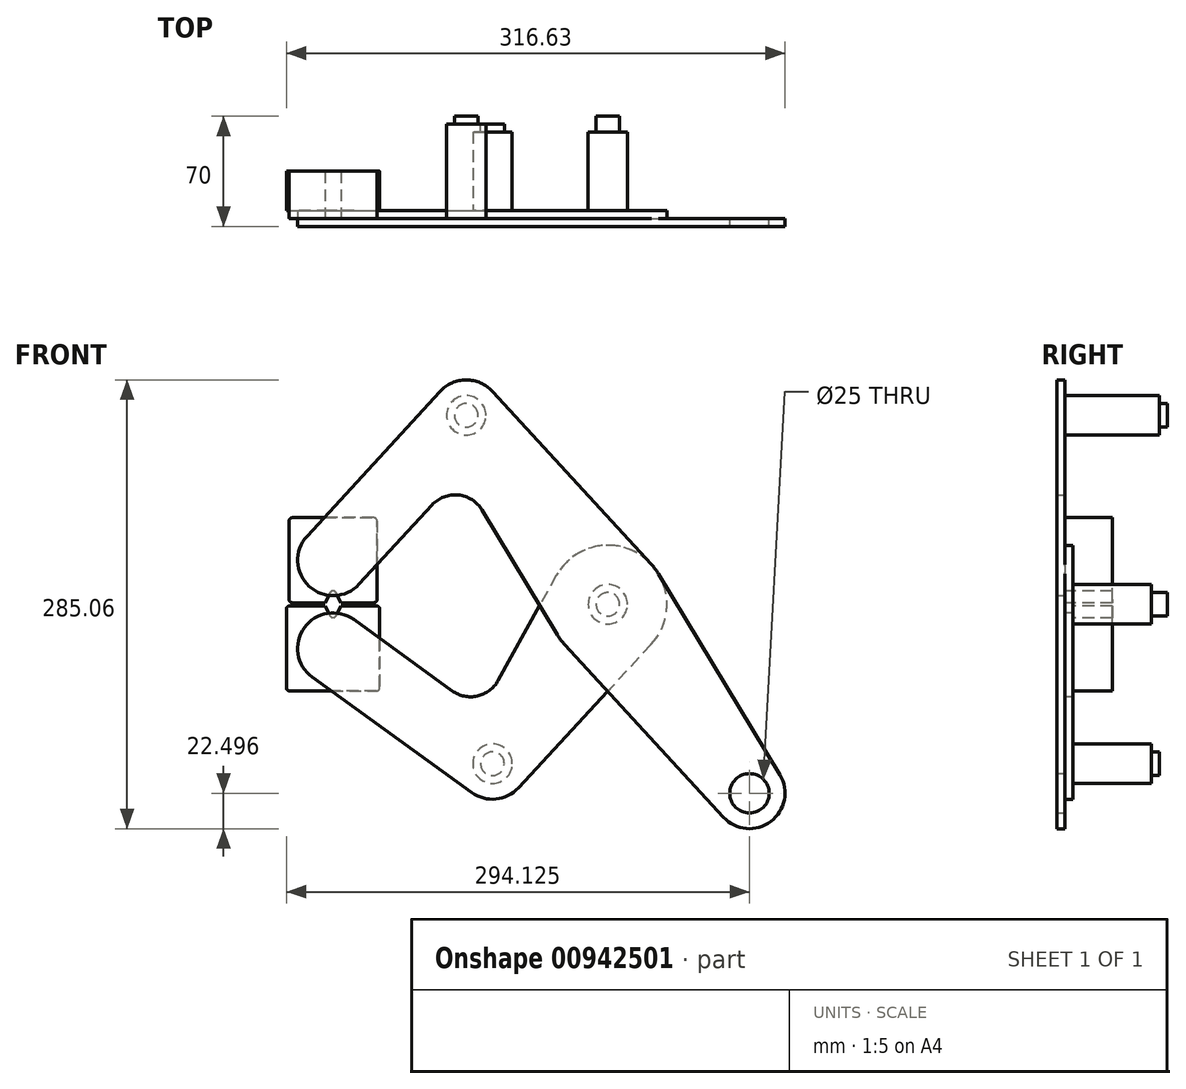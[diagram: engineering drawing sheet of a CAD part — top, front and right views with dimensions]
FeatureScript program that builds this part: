
annotation { "Feature Type Name" : "Feature", "Feature Type Description" : "" }
export const myFeature = defineFeature(function(context is Context, id is Id, definition is map)
    precondition{}
    {
        {
            var Q0;
            Q0=qCreatedBy(makeId("Front.planeOp"),FACE);
            var sketch = newSketch(context, id + "F0", { "sketchPlane" : qUnion([Q0])});
            skCircle(sketch, "E0", {"center": v(0, 0) * mm, "radius": 7.5 * mm});
            skCircle(sketch, "E1", {"center": v(89.96, -120.03) * mm, "radius": 7.5 * mm});
            skCircle(sketch, "E2", {"center": v(-89.96, 120.03) * mm, "radius": 7.5 * mm});
            skCircle(sketch, "E3", {"center": v(-174.54, 28) * mm, "radius": 7.5 * mm});
            skLineSegment(sketch, "E4", {"start": v(-89.96, 120.03) * mm, "end": v(-174.54, 28) * mm, "construction": true});
            skCircle(sketch, "E5", {"center": v(89.96, -120.03) * mm, "radius": 22.5 * mm});
            skCircle(sketch, "E6", {"center": v(-174.54, 28) * mm, "radius": 22.5 * mm});
            skCircle(sketch, "E7", {"center": v(-89.96, 120.03) * mm, "radius": 22.5 * mm});
            skLineSegment(sketch, "E8", {"start": v(-191.11, 43.23) * mm, "end": v(-106.52, 135.26) * mm});
            skLineSegment(sketch, "E9", {"start": v(-157.98, 12.78) * mm, "end": v(-111.77, 63.05) * mm});
            skCircle(sketch, "E10", {"center": v(0, 0) * mm, "radius": 37.5 * mm});
            skLineSegment(sketch, "E11", {"start": v(-73.39, 135.26) * mm, "end": v(27.6, 25.38) * mm});
            skLineSegment(sketch, "E12", {"start": v(-79.92, 59.85) * mm, "end": v(-32.1, -19.38) * mm});
            skLineSegment(sketch, "E13", {"start": v(-27.6, -25.38) * mm, "end": v(73.39, -135.26) * mm});
            skLineSegment(sketch, "E14", {"start": v(32.1, 19.38) * mm, "end": v(109.22, -108.4) * mm});
            skArc(sketch, "E15.filletArc", {"start": v(-79.92, 59.85) * mm, "mid": v(-95.04, 69.42) * mm, "end": v(-111.77, 63.05) * mm});
            skLineSegment(sketch, "E16", {"start": v(0, 0) * mm, "end": v(-73.27, -101.27) * mm, "construction": true});
            skLineSegment(sketch, "E17", {"start": v(-73.27, -101.27) * mm, "end": v(-174.54, -28) * mm, "construction": true});
            skCircle(sketch, "E18", {"center": v(-174.54, -28) * mm, "radius": 7.5 * mm});
            skCircle(sketch, "E19", {"center": v(-73.27, -101.27) * mm, "radius": 7.5 * mm});
            skCircle(sketch, "E20", {"center": v(-174.54, -28) * mm, "radius": 22.5 * mm});
            skCircle(sketch, "E21", {"center": v(-73.27, -101.27) * mm, "radius": 22.5 * mm});
            skLineSegment(sketch, "E22", {"start": v(-161.36, -9.77) * mm, "end": v(-98.93, -54.94) * mm});
            skLineSegment(sketch, "E23", {"start": v(-187.73, -46.23) * mm, "end": v(-86.46, -119.5) * mm});
            skLineSegment(sketch, "E24", {"start": v(-32.8, 18.18) * mm, "end": v(-69.71, -48.43) * mm});
            skLineSegment(sketch, "E25", {"start": v(27.52, -25.47) * mm, "end": v(-56.76, -116.55) * mm});
            skArc(sketch, "E26.filletArc", {"start": v(-98.93, -54.94) * mm, "mid": v(-82.85, -58.26) * mm, "end": v(-69.71, -48.43) * mm});
            skLineSegment(sketch, "E27", {"start": v(-89.96, 120.03) * mm, "end": v(89.96, -120.03) * mm, "construction": true});
            skLineSegment(sketch, "E28", {"start": v(0, 0) * mm, "end": v(-145.88, 0) * mm, "construction": true});
            skCircle(sketch, "E29", {"center": v(0, 0) * mm, "radius": 12.5 * mm});
            skCircle(sketch, "E30", {"center": v(89.96, -120.03) * mm, "radius": 12.5 * mm});
            skCircle(sketch, "E31", {"center": v(-73.27, -101.27) * mm, "radius": 12.5 * mm});
            skCircle(sketch, "E32", {"center": v(-89.96, 120.03) * mm, "radius": 12.5 * mm});
            skSolve(sketch);
        }
        {
            assignVariable(context, id + "F1", {"name" : "offsetdx", "anyValue" : 35});
        }
        {
            var Q0;
            {var subQ0=sQuery(id+"F0.wireOp",EDGE,"E8");Q0=makeQuery(id+"F0.imprint","IMPRINT",FACE,{"disambiguationData":[TD([[makeQuery(id+"F0.imprint","IMPRINT",EDGE,{"derivedFrom":subQ0}),-1.0]])]});}
            var Q1;
            Q1=makeQuery(id+"F0.imprint","IMPRINT",FACE,{"disambiguationData":[TD([[makeQuery(id+"F0.imprint","IMPRINT",EDGE,{"derivedFrom":sQuery(id+"F0.wireOp",EDGE,"E32")}),-1.0]])]});
            var Q2;
            Q2=makeQuery(id+"F0.imprint","IMPRINT",FACE,{"disambiguationData":[TD([[makeQuery(id+"F0.imprint","IMPRINT",EDGE,{"derivedFrom":sQuery(id+"F0.wireOp",EDGE,"E3")}),-1.0]])]});
            var Q3;
            Q3=makeQuery(id+"F0.imprint","IMPRINT",FACE,{"disambiguationData":[TD([[makeQuery(id+"F0.imprint","IMPRINT",EDGE,{"derivedFrom":sQuery(id+"F0.wireOp",EDGE,"E29")}),-1.0]])]});
            var Q4;
            {var subQ0=sQuery(id+"F0.wireOp",EDGE,"E13");var subQ1=sQuery(id+"F0.wireOp",EDGE,"E10");var subQ2=makeQuery(id+"F0.imprint","INTERSECT",VERTEX,{"derivedFrom":[subQ1,subQ0]});Q4=makeQuery(id+"F0.imprint","IMPRINT",FACE,{"disambiguationData":[TD([[makeQuery(id+"F0.imprint","IMPRINT",EDGE,{"disambiguationData":[TD([[subQ2,-1.0]])],"derivedFrom":subQ1}),-1.0]])]});}
            var Q5;
            {var subQ0=sQuery(id+"F0.wireOp",EDGE,"E14");Q5=makeQuery(id+"F0.imprint","IMPRINT",FACE,{"disambiguationData":[TD([[makeQuery(id+"F0.imprint","IMPRINT",EDGE,{"derivedFrom":subQ0}),-1.0]])]});}
            var Q6;
            Q6=makeQuery(id+"F0.imprint","IMPRINT",FACE,{"disambiguationData":[TD([[makeQuery(id+"F0.imprint","IMPRINT",EDGE,{"derivedFrom":sQuery(id+"F0.wireOp",EDGE,"E30")}),-1.0]])]});
            var Q7;
            {var subQ0=sQuery(id+"F0.wireOp",EDGE,"E12");var subQ1=sQuery(id+"F0.wireOp",EDGE,"E10");var subQ2=makeQuery(id+"F0.imprint","INTERSECT",VERTEX,{"derivedFrom":[subQ1,subQ0]});Q7=makeQuery(id+"F0.imprint","IMPRINT",FACE,{"disambiguationData":[TD([[makeQuery(id+"F0.imprint","IMPRINT",EDGE,{"disambiguationData":[TD([[subQ2,1.0]])],"derivedFrom":subQ1}),-1.0]])]});}
            var Q8;
            Q8=makeQuery(id+"F0.imprint","IMPRINT",FACE,{"disambiguationData":[TD([[makeQuery(id+"F0.imprint","IMPRINT",EDGE,{"derivedFrom":sQuery(id+"F0.wireOp",EDGE,"E0")}),-1.0]])]});
            var Q9;
            Q9=makeQuery(id+"F0.imprint","IMPRINT",FACE,{"disambiguationData":[TD([[makeQuery(id+"F0.imprint","IMPRINT",EDGE,{"derivedFrom":sQuery(id+"F0.wireOp",EDGE,"E2")}),-1.0]])]});
            extrude(context, id + "F2", {"entities" : qUnion([Q0, Q1, Q2, Q3, Q4, Q5, Q6, Q7, Q8, Q9]), "depth" : 5 * mm, "offsetDistance" : 25 * mm});
        }
        {
            var Q0;
            {var subQ0=sQuery(id+"F0.wireOp",EDGE,"E22");Q0=makeQuery(id+"F0.imprint","IMPRINT",FACE,{"disambiguationData":[TD([[makeQuery(id+"F0.imprint","IMPRINT",EDGE,{"derivedFrom":subQ0}),-1.0]])]});}
            var Q1;
            Q1=makeQuery(id+"F0.imprint","IMPRINT",FACE,{"disambiguationData":[TD([[makeQuery(id+"F0.imprint","IMPRINT",EDGE,{"derivedFrom":sQuery(id+"F0.wireOp",EDGE,"E29")}),-1.0]])]});
            var Q2;
            {var subQ0=sQuery(id+"F0.wireOp",EDGE,"E13");var subQ1=sQuery(id+"F0.wireOp",EDGE,"E10");var subQ2=makeQuery(id+"F0.imprint","INTERSECT",VERTEX,{"derivedFrom":[subQ1,subQ0]});Q2=makeQuery(id+"F0.imprint","IMPRINT",FACE,{"disambiguationData":[TD([[makeQuery(id+"F0.imprint","IMPRINT",EDGE,{"disambiguationData":[TD([[subQ2,-1.0]])],"derivedFrom":subQ1}),-1.0]])]});}
            var Q3;
            Q3=makeQuery(id+"F0.imprint","IMPRINT",FACE,{"disambiguationData":[TD([[makeQuery(id+"F0.imprint","IMPRINT",EDGE,{"derivedFrom":sQuery(id+"F0.wireOp",EDGE,"E31")}),-1.0]])]});
            var Q4;
            Q4=makeQuery(id+"F0.imprint","IMPRINT",FACE,{"disambiguationData":[TD([[makeQuery(id+"F0.imprint","IMPRINT",EDGE,{"derivedFrom":sQuery(id+"F0.wireOp",EDGE,"E18")}),-1.0]])]});
            var Q5;
            {var subQ0=sQuery(id+"F0.wireOp",EDGE,"E12");var subQ1=sQuery(id+"F0.wireOp",EDGE,"E10");var subQ2=makeQuery(id+"F0.imprint","INTERSECT",VERTEX,{"derivedFrom":[subQ1,subQ0]});Q5=makeQuery(id+"F0.imprint","IMPRINT",FACE,{"disambiguationData":[TD([[makeQuery(id+"F0.imprint","IMPRINT",EDGE,{"disambiguationData":[TD([[subQ2,1.0]])],"derivedFrom":subQ1}),-1.0]])]});}
            var Q6;
            Q6=makeQuery(id+"F0.imprint","IMPRINT",FACE,{"disambiguationData":[TD([[makeQuery(id+"F0.imprint","IMPRINT",EDGE,{"derivedFrom":sQuery(id+"F0.wireOp",EDGE,"E19")}),-1.0]])]});
            var Q7;
            Q7=makeQuery(id+"F0.imprint","IMPRINT",FACE,{"disambiguationData":[TD([[makeQuery(id+"F0.imprint","IMPRINT",EDGE,{"derivedFrom":sQuery(id+"F0.wireOp",EDGE,"E0")}),-1.0]])]});
            extrude(context, id + "F3", {"entities" : qUnion([Q0, Q1, Q2, Q3, Q4, Q5, Q6, Q7]), "oppositeDirection" : true, "depth" : 5 * mm, "offsetDistance" : 25 * mm});
        }
        {
            var Q0;
            {var subQ0=sQuery(id+"F0.wireOp",EDGE,"E8");Q0=makeQuery(id+"F0.imprint","IMPRINT",FACE,{"disambiguationData":[TD([[makeQuery(id+"F0.imprint","IMPRINT",EDGE,{"derivedFrom":subQ0}),-1.0]])]});}
            var sketch = newSketch(context, id + "F4", { "sketchPlane" : qUnion([Q0])});
            skLineSegment(sketch, "E33.0", {"start": v(0, 0) * mm, "end": v(-145.88, 0) * mm});
            skPoint(sketch, "E34.0", {"position": v(-174.54, 28) * mm});
            skLineSegment(sketch, "E35", {"start": v(-174.54, 28) * mm, "end": v(-174.54, 1) * mm, "construction": true});
            skLineSegment(sketch, "E36.bottom", {"start": v(-202.44, 55) * mm, "end": v(-146.65, 55) * mm});
            skLineSegment(sketch, "E36.top", {"start": v(-202.44, 1) * mm, "end": v(-146.65, 1) * mm});
            skLineSegment(sketch, "E36.left", {"start": v(-202.44, 55) * mm, "end": v(-202.44, 1) * mm});
            skLineSegment(sketch, "E36.right", {"start": v(-146.65, 55) * mm, "end": v(-146.65, 1) * mm});
            skLineSegment(sketch, "E37", {"start": v(-174.54, 11) * mm, "end": v(-169.54, 1) * mm});
            skLineSegment(sketch, "E38", {"start": v(-174.54, 11) * mm, "end": v(-179.54, 1) * mm});
            skLineSegment(sketch, "E39", {"start": v(-179.54, 1) * mm, "end": v(-169.54, 1) * mm});
            skSolve(sketch);
        }
        {
            var Q0;
            Q0=makeQuery(id+"F3.opExtrude","CAP_FACE",FACE,{"disambiguationData":[OSD([sQuery(id+"F0.wireOp",EDGE,"E10"),sQuery(id+"F0.wireOp",EDGE,"E18"),sQuery(id+"F0.wireOp",EDGE,"E20"),sQuery(id+"F0.wireOp",EDGE,"E21"),sQuery(id+"F0.wireOp",EDGE,"E22"),sQuery(id+"F0.wireOp",EDGE,"E23"),sQuery(id+"F0.wireOp",EDGE,"E24"),sQuery(id+"F0.wireOp",EDGE,"E25"),sQuery(id+"F0.wireOp",EDGE,"E26.filletArc"),sQuery(id+"F0.wireOp",EDGE,"E29"),sQuery(id+"F0.wireOp",EDGE,"E31")])],"isStart":false});
            var sketch = newSketch(context, id + "F5", { "sketchPlane" : qUnion([Q0])});
            skCircle(sketch, "E40.0", {"center": v(174.54, -28) * mm, "radius": 7.5 * mm});
            skLineSegment(sketch, "E41.bottom", {"start": v(204.17, -1) * mm, "end": v(144.92, -1) * mm});
            skLineSegment(sketch, "E41.top", {"start": v(204.17, -55) * mm, "end": v(144.92, -55) * mm});
            skLineSegment(sketch, "E41.left", {"start": v(204.17, -1) * mm, "end": v(204.17, -55) * mm});
            skLineSegment(sketch, "E41.right", {"start": v(144.92, -1) * mm, "end": v(144.92, -55) * mm});
            skLineSegment(sketch, "E42", {"start": v(174.54, -28) * mm, "end": v(174.54, -1) * mm, "construction": true});
            skLineSegment(sketch, "E43", {"start": v(174.54, -11) * mm, "end": v(169.54, -1) * mm});
            skLineSegment(sketch, "E44", {"start": v(174.54, -11) * mm, "end": v(179.54, -1) * mm});
            skSolve(sketch);
        }
        {
            var Q0;
            Q0=makeQuery(id+"F2.opExtrude","CAP_FACE",FACE,{"disambiguationData":[OSD([sQuery(id+"F0.wireOp",EDGE,"E3"),sQuery(id+"F0.wireOp",EDGE,"E5"),sQuery(id+"F0.wireOp",EDGE,"E6"),sQuery(id+"F0.wireOp",EDGE,"E7"),sQuery(id+"F0.wireOp",EDGE,"E8"),sQuery(id+"F0.wireOp",EDGE,"E9"),sQuery(id+"F0.wireOp",EDGE,"E10"),sQuery(id+"F0.wireOp",EDGE,"E11"),sQuery(id+"F0.wireOp",EDGE,"E12"),sQuery(id+"F0.wireOp",EDGE,"E13"),sQuery(id+"F0.wireOp",EDGE,"E14"),sQuery(id+"F0.wireOp",EDGE,"E15.filletArc"),sQuery(id+"F0.wireOp",EDGE,"E29"),sQuery(id+"F0.wireOp",EDGE,"E30"),sQuery(id+"F0.wireOp",EDGE,"E32")])],"isStart":false});
            cPlane(context, id + "F6", {"entities" : qUnion([Q0]), "cplaneType" : CPlaneType.OFFSET, "offset" : (getVariable(context, 'offsetdx')) * mm, "oppositeDirection" : true, "width" : 150 * mm, "height" : 150 * mm});
        }
        {
            var Q0;
            Q0=makeQuery(id+"F0.imprint","IMPRINT",FACE,{"disambiguationData":[TD([[makeQuery(id+"F0.imprint","IMPRINT",EDGE,{"derivedFrom":sQuery(id+"F0.wireOp",EDGE,"E0")}),-1.0]])]});
            var Q1;
            Q1=makeQuery(id+"F0.imprint","IMPRINT",FACE,{"disambiguationData":[TD([[makeQuery(id+"F0.imprint","IMPRINT",EDGE,{"derivedFrom":sQuery(id+"F0.wireOp",EDGE,"E2")}),-1.0]])]});
            var Q2;
            Q2=qCreatedBy(id+"F6.planeOp",FACE);
            var Q3;
            Q3=makeQuery(id+"F2.opExtrude","CAP_FACE",FACE,{"disambiguationData":[OSD([sQuery(id+"F0.wireOp",EDGE,"E3"),sQuery(id+"F0.wireOp",EDGE,"E5"),sQuery(id+"F0.wireOp",EDGE,"E6"),sQuery(id+"F0.wireOp",EDGE,"E7"),sQuery(id+"F0.wireOp",EDGE,"E8"),sQuery(id+"F0.wireOp",EDGE,"E9"),sQuery(id+"F0.wireOp",EDGE,"E10"),sQuery(id+"F0.wireOp",EDGE,"E11"),sQuery(id+"F0.wireOp",EDGE,"E12"),sQuery(id+"F0.wireOp",EDGE,"E13"),sQuery(id+"F0.wireOp",EDGE,"E14"),sQuery(id+"F0.wireOp",EDGE,"E15.filletArc"),sQuery(id+"F0.wireOp",EDGE,"E29"),sQuery(id+"F0.wireOp",EDGE,"E30"),sQuery(id+"F0.wireOp",EDGE,"E32")])],"isStart":false});
            extrude(context, id + "F7", {"entities" : qUnion([Q0, Q1]), "endBound" : BoundingType.UP_TO_SURFACE, "oppositeDirection" : true, "depth" : 25 * mm, "endBoundEntityFace" : qUnion([Q2]), "offsetDistance" : 25 * mm, "hasSecondDirection" : true, "secondDirectionBound" : SecondDirectionBoundingType.UP_TO_SURFACE, "secondDirectionOppositeDirection" : false, "secondDirectionDepth" : 25 * mm, "secondDirectionBoundEntityFace" : qUnion([Q3])});
        }
        {
            var Q0;
            Q0=makeQuery(id+"F0.imprint","IMPRINT",FACE,{"disambiguationData":[TD([[makeQuery(id+"F0.imprint","IMPRINT",EDGE,{"derivedFrom":sQuery(id+"F0.wireOp",EDGE,"E19")}),-1.0]])]});
            var Q1;
            Q1=qCreatedBy(id+"F6.planeOp",FACE);
            extrude(context, id + "F8", {"entities" : qUnion([Q0]), "endBound" : BoundingType.UP_TO_SURFACE, "oppositeDirection" : true, "depth" : 25 * mm, "endBoundEntityFace" : qUnion([Q1]), "offsetDistance" : 25 * mm});
        }
        {
            var Q0;
            {var subQ0=sQuery(id+"F4.wireOp",EDGE,"E36.left");Q0=makeQuery(id+"F4.imprint","IMPRINT",FACE,{"disambiguationData":[TD([[makeQuery(id+"F4.imprint","IMPRINT",EDGE,{"derivedFrom":subQ0}),1.0]])]});}
            var Q1;
            {var subQ4=sQuery(id+"F4.wireOp",EDGE,"E36.right");var subQ5=sQuery(id+"F4.wireOp",EDGE,"E36.bottom");var subQ6=makeQuery(id+"F4.imprint","INTERSECT",VERTEX,{"derivedFrom":[subQ5,subQ4]});Q1=makeQuery(id+"F4.imprint","IMPRINT",FACE,{"disambiguationData":[TD([[makeQuery(id+"F4.imprint","IMPRINT",EDGE,{"disambiguationData":[TD([[subQ6,1.0]])],"derivedFrom":subQ5}),-1.0]])]});}
            var Q2;
            Q2=qCreatedBy(id+"F6.planeOp",FACE);
            extrude(context, id + "F9", {"entities" : qUnion([Q0, Q1]), "endBound" : BoundingType.UP_TO_SURFACE, "oppositeDirection" : true, "depth" : 25 * mm, "endBoundEntityFace" : qUnion([Q2]), "offsetDistance" : 25 * mm});
        }
        {
            var Q0;
            Q0=makeQuery(id+"F0.imprint","IMPRINT",FACE,{"disambiguationData":[TD([[makeQuery(id+"F0.imprint","IMPRINT",EDGE,{"derivedFrom":sQuery(id+"F0.wireOp",EDGE,"E3")}),1.0]])]});
            var Q1;
            Q1=makeQuery(id+"F2.opExtrude","CAP_FACE",FACE,{"disambiguationData":[OSD([sQuery(id+"F0.wireOp",EDGE,"E3"),sQuery(id+"F0.wireOp",EDGE,"E5"),sQuery(id+"F0.wireOp",EDGE,"E6"),sQuery(id+"F0.wireOp",EDGE,"E7"),sQuery(id+"F0.wireOp",EDGE,"E8"),sQuery(id+"F0.wireOp",EDGE,"E9"),sQuery(id+"F0.wireOp",EDGE,"E10"),sQuery(id+"F0.wireOp",EDGE,"E11"),sQuery(id+"F0.wireOp",EDGE,"E12"),sQuery(id+"F0.wireOp",EDGE,"E13"),sQuery(id+"F0.wireOp",EDGE,"E14"),sQuery(id+"F0.wireOp",EDGE,"E15.filletArc"),sQuery(id+"F0.wireOp",EDGE,"E29"),sQuery(id+"F0.wireOp",EDGE,"E30"),sQuery(id+"F0.wireOp",EDGE,"E32")])],"isStart":false});
            extrude(context, id + "F10", {"entities" : qUnion([Q0]), "operationType" : NewBodyOperationType.ADD, "endBound" : BoundingType.UP_TO_SURFACE, "depth" : 25 * mm, "endBoundEntityFace" : qUnion([Q1]), "offsetDistance" : 25 * mm});
        }
        {
            var Q0;
            Q0=makeQuery(id+"F5.imprint","IMPRINT",FACE,{"disambiguationData":[TD([[makeQuery(id+"F5.imprint","IMPRINT",EDGE,{"derivedFrom":sQuery(id+"F5.wireOp",EDGE,"E40.0")}),1.0]])]});
            var Q1;
            {var subQ5=sQuery(id+"F5.wireOp",EDGE,"E41.left");Q1=makeQuery(id+"F5.imprint","IMPRINT",FACE,{"disambiguationData":[TD([[makeQuery(id+"F5.imprint","IMPRINT",EDGE,{"derivedFrom":subQ5}),-1.0]])]});}
            var Q2;
            {var subQ5=sQuery(id+"F5.wireOp",EDGE,"E41.bottom");var subQ7=sQuery(id+"F5.wireOp",EDGE,"E41.right");var subQ8=makeQuery(id+"F5.imprint","INTERSECT",VERTEX,{"derivedFrom":[subQ5,subQ7]});Q2=makeQuery(id+"F5.imprint","IMPRINT",FACE,{"disambiguationData":[TD([[makeQuery(id+"F5.imprint","IMPRINT",EDGE,{"disambiguationData":[TD([[subQ8,1.0]])],"derivedFrom":subQ5}),1.0]])]});}
            var Q3;
            Q3=makeQuery(id+"F5.imprint","IMPRINT",FACE,{"disambiguationData":[TD([[makeQuery(id+"F5.imprint","IMPRINT",EDGE,{"derivedFrom":sQuery(id+"F5.wireOp",EDGE,"E40.0")}),-1.0]])]});
            var Q4;
            Q4=qCreatedBy(id+"F6.planeOp",FACE);
            extrude(context, id + "F11", {"entities" : qUnion([Q0, Q1, Q2, Q3]), "endBound" : BoundingType.UP_TO_SURFACE, "depth" : 25 * mm, "endBoundEntityFace" : qUnion([Q4]), "offsetDistance" : 25 * mm});
        }
        {
            var Q0;
            Q0=makeQuery(id+"F0.imprint","IMPRINT",FACE,{"disambiguationData":[TD([[makeQuery(id+"F0.imprint","IMPRINT",EDGE,{"derivedFrom":sQuery(id+"F0.wireOp",EDGE,"E18")}),1.0]])]});
            var Q1;
            Q1=makeQuery(id+"F11.opExtrude","CAP_FACE",FACE,{"disambiguationData":[OSD([sQuery(id+"F5.wireOp",EDGE,"E41.bottom"),sQuery(id+"F5.wireOp",EDGE,"E41.top"),sQuery(id+"F5.wireOp",EDGE,"E41.left"),sQuery(id+"F5.wireOp",EDGE,"E41.right"),sQuery(id+"F5.wireOp",EDGE,"E43"),sQuery(id+"F5.wireOp",EDGE,"E44")])],"isStart":true});
            extrude(context, id + "F12", {"entities" : qUnion([Q0]), "operationType" : NewBodyOperationType.ADD, "endBound" : BoundingType.UP_TO_SURFACE, "oppositeDirection" : true, "depth" : 25 * mm, "endBoundEntityFace" : qUnion([Q1]), "offsetDistance" : 25 * mm});
        }
        {
            var Q0;
            Q0=makeQuery(id+"F8.opExtrude","SWEPT_BODY",BODY,{"disambiguationData":[OSD([sQuery(id+"F0.wireOp",EDGE,"E19"),sQuery(id+"F0.wireOp",EDGE,"E31")])]});
            var Q1;
            Q1=makeQuery(id+"F7.opExtrude","SWEPT_BODY",BODY,{"disambiguationData":[OSD([sQuery(id+"F0.wireOp",EDGE,"E2"),sQuery(id+"F0.wireOp",EDGE,"E32")])]});
            deleteBodies(context, id + "F13", {"entities" : qUnion([Q0, Q1])});
        }
        {
            var Q0;
            Q0=makeQuery(id+"F7.opExtrude","SWEPT_BODY",BODY,{"disambiguationData":[OSD([sQuery(id+"F0.wireOp",EDGE,"E0"),sQuery(id+"F0.wireOp",EDGE,"E29")])]});
            deleteBodies(context, id + "F14", {"entities" : qUnion([Q0])});
        }
        {
            var Q0;
            Q0=makeQuery(id+"F0.imprint","IMPRINT",FACE,{"disambiguationData":[TD([[makeQuery(id+"F0.imprint","IMPRINT",EDGE,{"derivedFrom":sQuery(id+"F0.wireOp",EDGE,"E2")}),-1.0]])]});
            var Q1;
            Q1=makeQuery(id+"F0.imprint","IMPRINT",FACE,{"disambiguationData":[TD([[makeQuery(id+"F0.imprint","IMPRINT",EDGE,{"derivedFrom":sQuery(id+"F0.wireOp",EDGE,"E2")}),1.0]])]});
            var Q2;
            Q2=makeQuery(id+"F0.imprint","IMPRINT",FACE,{"disambiguationData":[TD([[makeQuery(id+"F0.imprint","IMPRINT",EDGE,{"derivedFrom":sQuery(id+"F0.wireOp",EDGE,"E0")}),1.0]])]});
            var Q3;
            Q3=makeQuery(id+"F0.imprint","IMPRINT",FACE,{"disambiguationData":[TD([[makeQuery(id+"F0.imprint","IMPRINT",EDGE,{"derivedFrom":sQuery(id+"F0.wireOp",EDGE,"E0")}),-1.0]])]});
            var Q4;
            Q4=qCreatedBy(id+"F6.planeOp",FACE);
            var Q5;
            Q5=makeQuery(id+"F2.opExtrude","CAP_FACE",FACE,{"disambiguationData":[OSD([sQuery(id+"F0.wireOp",EDGE,"E3"),sQuery(id+"F0.wireOp",EDGE,"E5"),sQuery(id+"F0.wireOp",EDGE,"E6"),sQuery(id+"F0.wireOp",EDGE,"E7"),sQuery(id+"F0.wireOp",EDGE,"E8"),sQuery(id+"F0.wireOp",EDGE,"E9"),sQuery(id+"F0.wireOp",EDGE,"E10"),sQuery(id+"F0.wireOp",EDGE,"E11"),sQuery(id+"F0.wireOp",EDGE,"E12"),sQuery(id+"F0.wireOp",EDGE,"E13"),sQuery(id+"F0.wireOp",EDGE,"E14"),sQuery(id+"F0.wireOp",EDGE,"E15.filletArc"),sQuery(id+"F0.wireOp",EDGE,"E29"),sQuery(id+"F0.wireOp",EDGE,"E30"),sQuery(id+"F0.wireOp",EDGE,"E32")])],"isStart":false});
            extrude(context, id + "F15", {"entities" : qUnion([Q0, Q1, Q2, Q3]), "endBound" : BoundingType.UP_TO_SURFACE, "oppositeDirection" : true, "depth" : 25 * mm, "endBoundEntityFace" : qUnion([Q4]), "offsetDistance" : 25 * mm, "hasSecondDirection" : true, "secondDirectionBound" : SecondDirectionBoundingType.UP_TO_SURFACE, "secondDirectionOppositeDirection" : false, "secondDirectionDepth" : 25 * mm, "secondDirectionBoundEntityFace" : qUnion([Q5])});
        }
        {
            var Q0;
            Q0=makeQuery(id+"F0.imprint","IMPRINT",FACE,{"disambiguationData":[TD([[makeQuery(id+"F0.imprint","IMPRINT",EDGE,{"derivedFrom":sQuery(id+"F0.wireOp",EDGE,"E19")}),1.0]])]});
            var Q1;
            Q1=makeQuery(id+"F0.imprint","IMPRINT",FACE,{"disambiguationData":[TD([[makeQuery(id+"F0.imprint","IMPRINT",EDGE,{"derivedFrom":sQuery(id+"F0.wireOp",EDGE,"E19")}),-1.0]])]});
            var Q2;
            Q2=qCreatedBy(id+"F6.planeOp",FACE);
            extrude(context, id + "F16", {"entities" : qUnion([Q0, Q1]), "endBound" : BoundingType.UP_TO_SURFACE, "oppositeDirection" : true, "depth" : 25 * mm, "endBoundEntityFace" : qUnion([Q2]), "offsetDistance" : 25 * mm});
        }
        {
            var Q0;
            Q0=makeQuery(id+"F2.opExtrude","SWEPT_BODY",BODY,{"disambiguationData":[OSD([sQuery(id+"F0.wireOp",EDGE,"E3"),sQuery(id+"F0.wireOp",EDGE,"E5"),sQuery(id+"F0.wireOp",EDGE,"E6"),sQuery(id+"F0.wireOp",EDGE,"E7"),sQuery(id+"F0.wireOp",EDGE,"E8"),sQuery(id+"F0.wireOp",EDGE,"E9"),sQuery(id+"F0.wireOp",EDGE,"E10"),sQuery(id+"F0.wireOp",EDGE,"E11"),sQuery(id+"F0.wireOp",EDGE,"E12"),sQuery(id+"F0.wireOp",EDGE,"E13"),sQuery(id+"F0.wireOp",EDGE,"E14"),sQuery(id+"F0.wireOp",EDGE,"E15.filletArc"),sQuery(id+"F0.wireOp",EDGE,"E29"),sQuery(id+"F0.wireOp",EDGE,"E30"),sQuery(id+"F0.wireOp",EDGE,"E32")])]});
            var Q1;
            Q1=makeQuery(id+"F3.opExtrude","SWEPT_BODY",BODY,{"disambiguationData":[OSD([sQuery(id+"F0.wireOp",EDGE,"E10"),sQuery(id+"F0.wireOp",EDGE,"E18"),sQuery(id+"F0.wireOp",EDGE,"E20"),sQuery(id+"F0.wireOp",EDGE,"E21"),sQuery(id+"F0.wireOp",EDGE,"E22"),sQuery(id+"F0.wireOp",EDGE,"E23"),sQuery(id+"F0.wireOp",EDGE,"E24"),sQuery(id+"F0.wireOp",EDGE,"E25"),sQuery(id+"F0.wireOp",EDGE,"E26.filletArc"),sQuery(id+"F0.wireOp",EDGE,"E29"),sQuery(id+"F0.wireOp",EDGE,"E31")])]});
            var Q2;
            Q2=makeQuery(id+"F15.opExtrude","SWEPT_BODY",BODY,{"disambiguationData":[OSD([sQuery(id+"F0.wireOp",EDGE,"E32")])]});
            var Q3;
            Q3=makeQuery(id+"F15.opExtrude","SWEPT_BODY",BODY,{"disambiguationData":[OSD([sQuery(id+"F0.wireOp",EDGE,"E29")])]});
            var Q4;
            Q4=makeQuery(id+"F16.opExtrude","SWEPT_BODY",BODY,{"disambiguationData":[OSD([sQuery(id+"F0.wireOp",EDGE,"E31")])]});
            booleanBodies(context, id + "F17", {"operationType" : BooleanOperationType.SUBTRACTION, "tools" : qUnion([Q0, Q1]), "targets" : qUnion([Q2, Q3, Q4]), "keepTools" : true});
        }
        {
            var Q0;
            Q0=makeQuery(id+"F7.opExtrude","SWEPT_BODY",BODY,{"disambiguationData":[OSD([sQuery(id+"F0.wireOp",EDGE,"E2"),sQuery(id+"F0.wireOp",EDGE,"E32")])]});
            var Q1;
            Q1=makeQuery(id+"F9.opExtrude","SWEPT_BODY",BODY,{"disambiguationData":[OSD([sQuery(id+"F4.wireOp",EDGE,"E36.bottom"),sQuery(id+"F4.wireOp",EDGE,"E36.top"),sQuery(id+"F4.wireOp",EDGE,"E36.left"),sQuery(id+"F4.wireOp",EDGE,"E36.right"),sQuery(id+"F4.wireOp",EDGE,"E37"),sQuery(id+"F4.wireOp",EDGE,"E38")])]});
            var Q2;
            Q2=makeQuery(id+"F11.opExtrude","SWEPT_BODY",BODY,{"disambiguationData":[OSD([sQuery(id+"F5.wireOp",EDGE,"E41.bottom"),sQuery(id+"F5.wireOp",EDGE,"E41.top"),sQuery(id+"F5.wireOp",EDGE,"E41.left"),sQuery(id+"F5.wireOp",EDGE,"E41.right"),sQuery(id+"F5.wireOp",EDGE,"E43"),sQuery(id+"F5.wireOp",EDGE,"E44")])]});
            var Q3;
            Q3=makeQuery(id+"F15.opExtrude","SWEPT_BODY",BODY,{"disambiguationData":[OSD([sQuery(id+"F0.wireOp",EDGE,"E32")])]});
            var Q4;
            Q4=makeQuery(id+"F15.opExtrude","SWEPT_BODY",BODY,{"disambiguationData":[OSD([sQuery(id+"F0.wireOp",EDGE,"E29")])]});
            var Q5;
            Q5=makeQuery(id+"F16.opExtrude","SWEPT_BODY",BODY,{"disambiguationData":[OSD([sQuery(id+"F0.wireOp",EDGE,"E31")])]});
            var Q6;
            Q6=makeQuery(id+"F9.opExtrude","CAP_FACE",FACE,{"disambiguationData":[OSD([sQuery(id+"F4.wireOp",EDGE,"E36.bottom"),sQuery(id+"F4.wireOp",EDGE,"E36.top"),sQuery(id+"F4.wireOp",EDGE,"E36.left"),sQuery(id+"F4.wireOp",EDGE,"E36.right"),sQuery(id+"F4.wireOp",EDGE,"E37"),sQuery(id+"F4.wireOp",EDGE,"E38")])],"isStart":false});
            mirror(context, id + "F18", {"operationType" : NewBodyOperationType.ADD, "entities" : qUnion([Q0, Q1, Q2, Q3, Q4, Q5]), "mirrorPlane" : qUnion([Q6])});
        }
        {
            var Q0;
            {var subQ0=makeQuery(id+"F9.opExtrude","SWEPT_EDGE",EDGE,{"disambiguationData":[OSD([sQuery(id+"F4.wireOp",EDGE,"E36.bottom"),sQuery(id+"F4.wireOp",EDGE,"E36.left")])]});Q0=makeQuery(id+"F18.boolean.opBoolean","MERGE",EDGE,{"derivedFrom":[subQ0,makeQuery(id+"F18.opPattern","COPY",EDGE,{"derivedFrom":subQ0,"instanceName":"1"})]});}
            var Q1;
            {var subQ0=makeQuery(id+"F9.opExtrude","SWEPT_EDGE",EDGE,{"disambiguationData":[OSD([sQuery(id+"F4.wireOp",EDGE,"E36.bottom"),sQuery(id+"F4.wireOp",EDGE,"E36.right")])]});Q1=makeQuery(id+"F18.boolean.opBoolean","MERGE",EDGE,{"derivedFrom":[subQ0,makeQuery(id+"F18.opPattern","COPY",EDGE,{"derivedFrom":subQ0,"instanceName":"1"})]});}
            var Q2;
            {var subQ0=makeQuery(id+"F9.opExtrude","SWEPT_EDGE",EDGE,{"disambiguationData":[OSD([sQuery(id+"F4.wireOp",EDGE,"E37"),sQuery(id+"F4.wireOp",EDGE,"E38")])]});Q2=makeQuery(id+"F18.boolean.opBoolean","MERGE",EDGE,{"derivedFrom":[subQ0,makeQuery(id+"F18.opPattern","COPY",EDGE,{"derivedFrom":subQ0,"instanceName":"1"})]});}
            var Q3;
            {var subQ0=makeQuery(id+"F9.opExtrude","SWEPT_EDGE",EDGE,{"disambiguationData":[OSD([sQuery(id+"F4.wireOp",EDGE,"E36.top"),sQuery(id+"F4.wireOp",EDGE,"E36.right")])]});Q3=makeQuery(id+"F18.boolean.opBoolean","MERGE",EDGE,{"derivedFrom":[subQ0,makeQuery(id+"F18.opPattern","COPY",EDGE,{"derivedFrom":subQ0,"instanceName":"1"})]});}
            var Q4;
            {var subQ0=makeQuery(id+"F9.opExtrude","SWEPT_EDGE",EDGE,{"disambiguationData":[OSD([sQuery(id+"F4.wireOp",EDGE,"E36.top"),sQuery(id+"F4.wireOp",EDGE,"E36.left")])]});Q4=makeQuery(id+"F18.boolean.opBoolean","MERGE",EDGE,{"derivedFrom":[subQ0,makeQuery(id+"F18.opPattern","COPY",EDGE,{"derivedFrom":subQ0,"instanceName":"1"})]});}
            var Q5;
            {var subQ0=makeQuery(id+"F11.opExtrude","SWEPT_EDGE",EDGE,{"disambiguationData":[OSD([sQuery(id+"F5.wireOp",EDGE,"E41.bottom"),sQuery(id+"F5.wireOp",EDGE,"E41.left")])]});Q5=makeQuery(id+"F18.boolean.opBoolean","MERGE",EDGE,{"derivedFrom":[subQ0,makeQuery(id+"F18.opPattern","COPY",EDGE,{"derivedFrom":subQ0,"instanceName":"1"})]});}
            var Q6;
            {var subQ0=makeQuery(id+"F11.opExtrude","SWEPT_EDGE",EDGE,{"disambiguationData":[OSD([sQuery(id+"F5.wireOp",EDGE,"E41.top"),sQuery(id+"F5.wireOp",EDGE,"E41.left")])]});Q6=makeQuery(id+"F18.boolean.opBoolean","MERGE",EDGE,{"derivedFrom":[subQ0,makeQuery(id+"F18.opPattern","COPY",EDGE,{"derivedFrom":subQ0,"instanceName":"1"})]});}
            var Q7;
            {var subQ0=makeQuery(id+"F11.opExtrude","SWEPT_EDGE",EDGE,{"disambiguationData":[OSD([sQuery(id+"F5.wireOp",EDGE,"E41.top"),sQuery(id+"F5.wireOp",EDGE,"E41.right")])]});Q7=makeQuery(id+"F18.boolean.opBoolean","MERGE",EDGE,{"derivedFrom":[subQ0,makeQuery(id+"F18.opPattern","COPY",EDGE,{"derivedFrom":subQ0,"instanceName":"1"})]});}
            var Q8;
            {var subQ0=makeQuery(id+"F11.opExtrude","SWEPT_EDGE",EDGE,{"disambiguationData":[OSD([sQuery(id+"F5.wireOp",EDGE,"E41.bottom"),sQuery(id+"F5.wireOp",EDGE,"E41.right")])]});Q8=makeQuery(id+"F18.boolean.opBoolean","MERGE",EDGE,{"derivedFrom":[subQ0,makeQuery(id+"F18.opPattern","COPY",EDGE,{"derivedFrom":subQ0,"instanceName":"1"})]});}
            var Q9;
            {var subQ0=makeQuery(id+"F11.opExtrude","SWEPT_EDGE",EDGE,{"disambiguationData":[OSD([sQuery(id+"F5.wireOp",EDGE,"E43"),sQuery(id+"F5.wireOp",EDGE,"E44")])]});Q9=makeQuery(id+"F18.boolean.opBoolean","MERGE",EDGE,{"derivedFrom":[subQ0,makeQuery(id+"F18.opPattern","COPY",EDGE,{"derivedFrom":subQ0,"instanceName":"1"})]});}
            fillet(context, id + "F19", {"entities" : qUnion([Q0, Q1, Q2, Q3, Q4, Q5, Q6, Q7, Q8, Q9]), "radius" : 2 * mm, "tangentPropagation" : true, "allowEdgeOverflow" : false});
        }
    });
